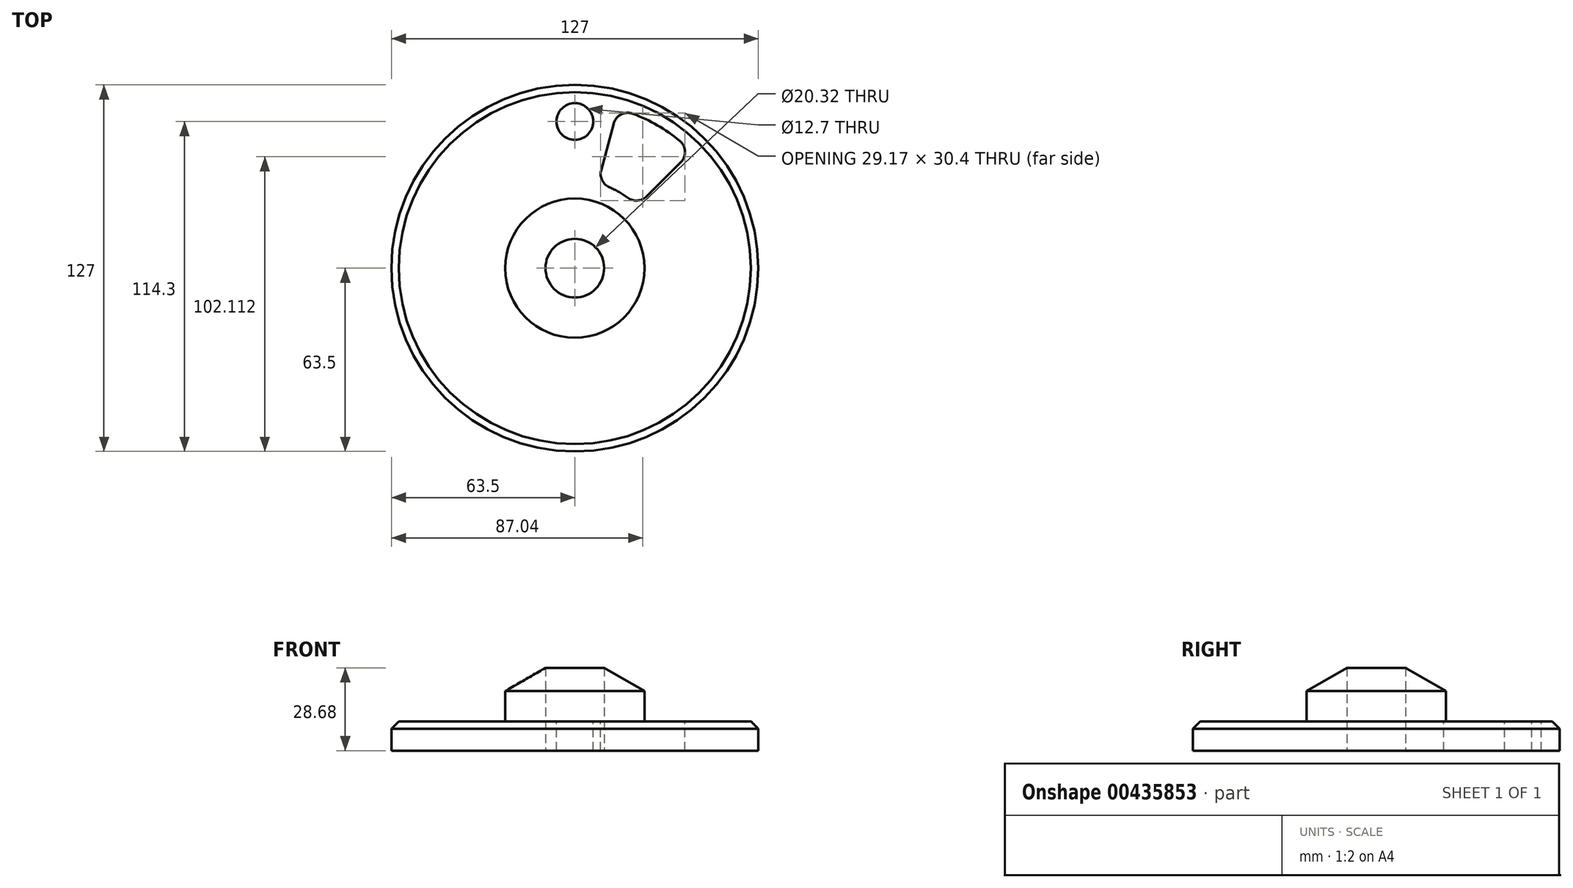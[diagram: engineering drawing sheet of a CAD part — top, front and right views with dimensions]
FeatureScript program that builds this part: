
annotation { "Feature Type Name" : "Feature", "Feature Type Description" : "" }
export const myFeature = defineFeature(function(context is Context, id is Id, definition is map)
    precondition{}
    {
        {
            var Q0;
            Q0=qCreatedBy(makeId("Front.planeOp"),FACE);
            var sketch = newSketch(context, id + "F0", { "sketchPlane" : qUnion([Q0])});
            skLineSegment(sketch, "E0", {"start": v(63.5, 0) * mm, "end": v(63.5, 10.16) * mm});
            skLineSegment(sketch, "E1", {"start": v(63.5, 10.16) * mm, "end": v(24.13, 10.16) * mm});
            skLineSegment(sketch, "E2", {"start": v(24.13, 10.16) * mm, "end": v(24.13, 20.61) * mm});
            skLineSegment(sketch, "E3", {"start": v(24.13, 20.61) * mm, "end": v(10.16, 28.68) * mm});
            skLineSegment(sketch, "E4", {"start": v(10.16, 28.68) * mm, "end": v(10.16, 0) * mm});
            skLineSegment(sketch, "E5", {"start": v(10.16, 0) * mm, "end": v(63.5, 0) * mm});
            skLineSegment(sketch, "E6", {"start": v(0, 0) * mm, "end": v(0, 19.32) * mm});
            skSolve(sketch);
        }
        {
            var Q0;
            Q0=makeQuery(id+"F0.imprint","IMPRINT",FACE,{"disambiguationData":[TD([[makeQuery(id+"F0.imprint","IMPRINT",EDGE,{"derivedFrom":sQuery(id+"F0.wireOp",EDGE,"E0")}),1.0]])]});
            var Q1;
            Q1=sQuery(id+"F0.wireOp",EDGE,"E6");
            revolve(context, id + "F1", {"entities" : qUnion([Q0]), "axis" : qUnion([Q1]), "revolveType" : RevolveType.FULL});
        }
        {
            var Q0;
            Q0=makeQuery(id+"F1.opRevolve","SWEPT_FACE",FACE,{"disambiguationData":[OSD([sQuery(id+"F0.wireOp",EDGE,"E1")])]});
            var sketch = newSketch(context, id + "F2", { "sketchPlane" : qUnion([Q0])});
            skPoint(sketch, "E7", {"position": v(0, 50.8) * mm});
            skSolve(sketch);
        }
        {
            var Q0;
            Q0=sQuery(id+"F2.wireOp",VERTEX,"E7");
            var Q1;
            Q1=makeQuery(id+"F1.opRevolve","SWEPT_BODY",BODY,{"disambiguationData":[OSD([sQuery(id+"F0.wireOp",EDGE,"E0"),sQuery(id+"F0.wireOp",EDGE,"E1"),sQuery(id+"F0.wireOp",EDGE,"E2"),sQuery(id+"F0.wireOp",EDGE,"E3"),sQuery(id+"F0.wireOp",EDGE,"E4"),sQuery(id+"F0.wireOp",EDGE,"E5")])]});
            hole(context, id + "F3", {"style" : HoleStyle.SIMPLE, "endStyle" : HoleEndStyle.THROUGH, "holeDiameter" : 12.7 * mm, "isTappedThrough" : true, "tappedDepth" : 12.7 * mm, "tapClearance" : 3, "locations" : qUnion([Q0]), "scope" : qUnion([Q1])});
        }
        {
            var Q0;
            Q0=makeQuery(id+"F1.opRevolve","SWEPT_FACE",FACE,{"disambiguationData":[OSD([sQuery(id+"F0.wireOp",EDGE,"E1")])]});
            var sketch = newSketch(context, id + "F4", { "sketchPlane" : qUnion([Q0])});
            skArc(sketch, "E8", {"start": v(21.55, 21.55) * mm, "mid": v(15.24, 26.4) * mm, "end": v(7.89, 29.44) * mm});
            skArc(sketch, "E9", {"start": v(40.41, 40.41) * mm, "mid": v(28.58, 49.5) * mm, "end": v(14.8, 55.2) * mm});
            skLineSegment(sketch, "E10", {"start": v(7.89, 29.44) * mm, "end": v(14.8, 55.2) * mm});
            skLineSegment(sketch, "E11", {"start": v(21.55, 21.55) * mm, "end": v(40.41, 40.41) * mm});
            skLineSegment(sketch, "E12", {"start": v(0, 0) * mm, "end": v(62.54, 108.32) * mm, "construction": true});
            skSolve(sketch);
        }
        {
            var Q0;
            Q0=makeQuery(id+"F4.imprint","IMPRINT",FACE,{"disambiguationData":[TD([[makeQuery(id+"F4.imprint","IMPRINT",EDGE,{"derivedFrom":sQuery(id+"F4.wireOp",EDGE,"E8")}),-1.0]])]});
            extrude(context, id + "F5", {"entities" : qUnion([Q0]), "operationType" : NewBodyOperationType.REMOVE, "endBound" : BoundingType.THROUGH_ALL, "oppositeDirection" : true, "depth" : 25.4 * mm});
        }
        {
            var Q0;
            Q0=makeQuery(id+"F5.boolean.opBoolean","COPY",EDGE,{"derivedFrom":makeQuery(id+"F5.opExtrude","SWEPT_EDGE",EDGE,{"disambiguationData":[OSD([sQuery(id+"F4.wireOp",EDGE,"E9"),sQuery(id+"F4.wireOp",EDGE,"E10")])]})});
            var Q1;
            Q1=makeQuery(id+"F5.boolean.opBoolean","COPY",EDGE,{"derivedFrom":makeQuery(id+"F5.opExtrude","SWEPT_EDGE",EDGE,{"disambiguationData":[OSD([sQuery(id+"F4.wireOp",EDGE,"E8"),sQuery(id+"F4.wireOp",EDGE,"E10")])]})});
            var Q2;
            Q2=makeQuery(id+"F5.boolean.opBoolean","COPY",EDGE,{"derivedFrom":makeQuery(id+"F5.opExtrude","SWEPT_EDGE",EDGE,{"disambiguationData":[OSD([sQuery(id+"F4.wireOp",EDGE,"E8"),sQuery(id+"F4.wireOp",EDGE,"E11")])]})});
            var Q3;
            Q3=makeQuery(id+"F5.boolean.opBoolean","COPY",EDGE,{"derivedFrom":makeQuery(id+"F5.opExtrude","SWEPT_EDGE",EDGE,{"disambiguationData":[OSD([sQuery(id+"F4.wireOp",EDGE,"E9"),sQuery(id+"F4.wireOp",EDGE,"E11")])]})});
            fillet(context, id + "F6", {"entities" : qUnion([Q0, Q1, Q2, Q3]), "radius" : 5.08 * mm, "tangentPropagation" : true, "allowEdgeOverflow" : false});
        }
        {
            var Q0;
            Q0=makeQuery(id+"F1.opRevolve","SWEPT_EDGE",EDGE,{"disambiguationData":[OSD([sQuery(id+"F0.wireOp",EDGE,"E0"),sQuery(id+"F0.wireOp",EDGE,"E1")])]});
            chamfer(context, id + "F7", {"entities" : qUnion([Q0]), "width" : 2.54 * mm, "tangentPropagation" : true});
        }
    });
